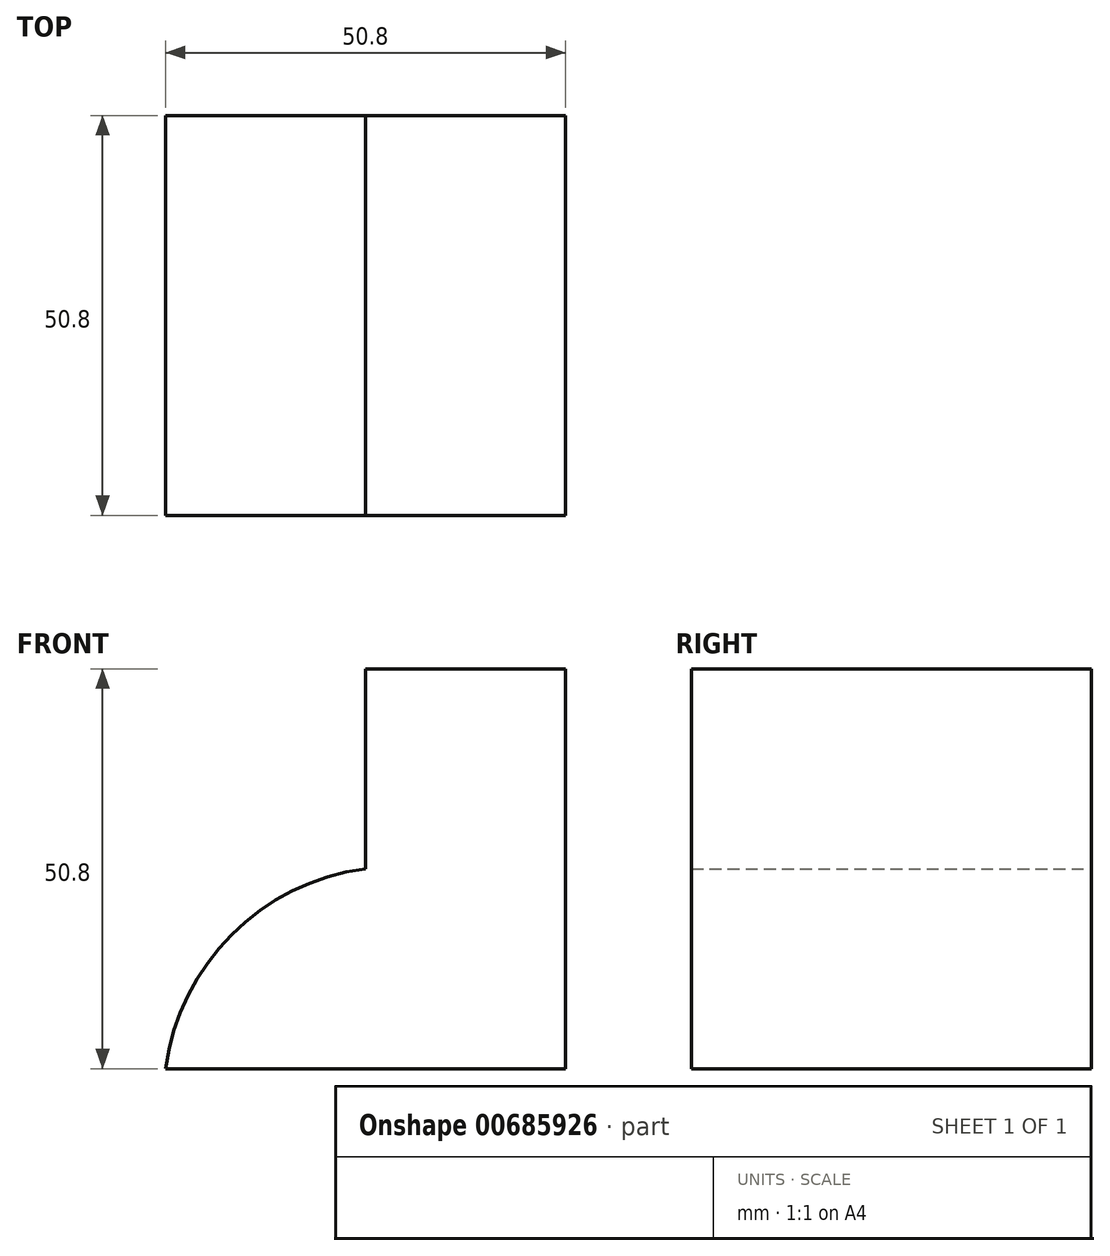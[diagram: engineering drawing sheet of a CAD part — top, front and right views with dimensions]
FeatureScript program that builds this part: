
annotation { "Feature Type Name" : "Feature", "Feature Type Description" : "" }
export const myFeature = defineFeature(function(context is Context, id is Id, definition is map)
    precondition{}
    {
        {
            var Q0;
            Q0=qCreatedBy(makeId("Front.planeOp"),FACE);
            var sketch = newSketch(context, id + "F0", { "sketchPlane" : qUnion([Q0])});
            skLineSegment(sketch, "E0", {"start": v(0, 0) * mm, "end": v(0, 25.4) * mm});
            skLineSegment(sketch, "E1", {"start": v(0, 25.4) * mm, "end": v(25.4, 25.4) * mm});
            skLineSegment(sketch, "E2", {"start": v(25.4, 25.4) * mm, "end": v(25.4, -25.4) * mm});
            skLineSegment(sketch, "E3", {"start": v(25.4, -25.4) * mm, "end": v(-25.4, -25.4) * mm});
            skArc(sketch, "E4", {"start": v(0, 0) * mm, "mid": v(-17.01, -8.39) * mm, "end": v(-25.4, -25.4) * mm});
            skSolve(sketch);
        }
        {
            var Q0;
            Q0 = qSketchRegion(id + "F0", true);
            extrude(context, id + "F1", {"entities" : qUnion([Q0]), "depth" : 50.8 * mm, "offsetDistance" : 25.4 * mm});
        }
    });
